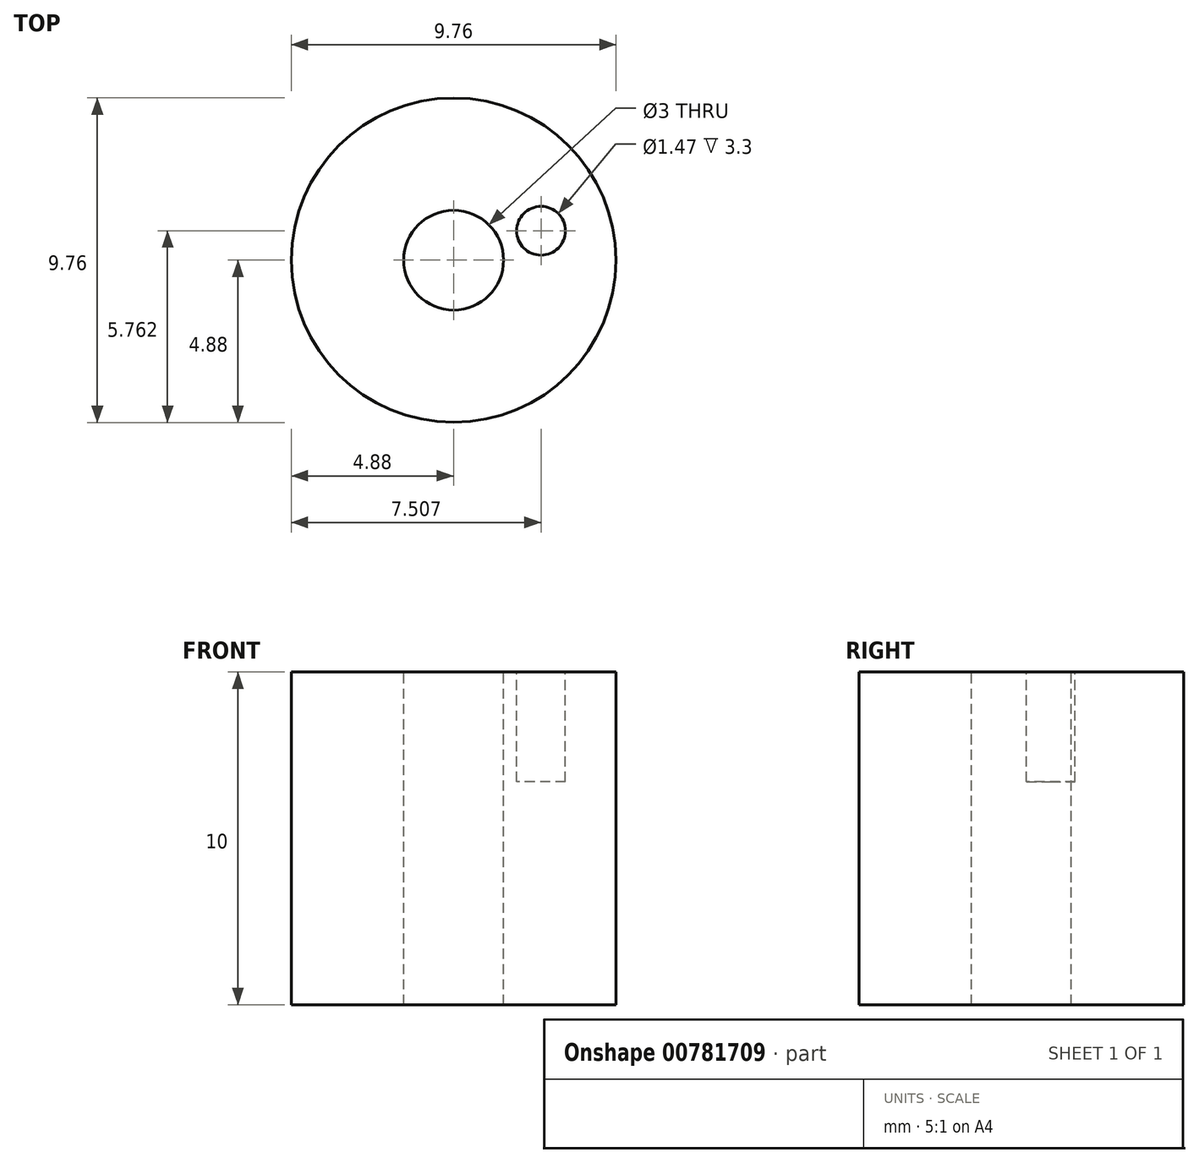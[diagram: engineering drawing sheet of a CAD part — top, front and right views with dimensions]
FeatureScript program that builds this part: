
annotation { "Feature Type Name" : "Feature", "Feature Type Description" : "" }
export const myFeature = defineFeature(function(context is Context, id is Id, definition is map)
    precondition{}
    {
        {
            var Q0;
            Q0=qCreatedBy(makeId("Top.planeOp"),FACE);
            var sketch = newSketch(context, id + "F0", { "sketchPlane" : qUnion([Q0])});
            skCircle(sketch, "E0", {"center": v(0, 0) * mm, "radius": 4.88 * mm});
            skSolve(sketch);
        }
        {
            var Q0;
            Q0=makeQuery(id+"F0.imprint","IMPRINT",FACE,{"disambiguationData":[TD([[makeQuery(id+"F0.imprint","IMPRINT",EDGE,{"derivedFrom":sQuery(id+"F0.wireOp",EDGE,"E0")}),1.0]])]});
            extrude(context, id + "F1", {"entities" : qUnion([Q0]), "depth" : 10 * mm, "offsetDistance" : 25.4 * mm});
        }
        {
            var Q0;
            Q0=makeQuery(id+"F1.opExtrude","CAP_FACE",FACE,{"disambiguationData":[OSD([sQuery(id+"F0.wireOp",EDGE,"E0")])],"isStart":false});
            var sketch = newSketch(context, id + "F2", { "sketchPlane" : qUnion([Q0])});
            skCircle(sketch, "E1", {"center": v(0, 0) * mm, "radius": 1.5 * mm});
            skSolve(sketch);
        }
        {
            var Q0;
            Q0=makeQuery(id+"F2.imprint","IMPRINT",FACE,{"disambiguationData":[TD([[makeQuery(id+"F2.imprint","IMPRINT",EDGE,{"derivedFrom":sQuery(id+"F2.wireOp",EDGE,"E1")}),1.0]])]});
            extrude(context, id + "F3", {"entities" : qUnion([Q0]), "operationType" : NewBodyOperationType.REMOVE, "oppositeDirection" : true, "depth" : 10 * mm, "offsetDistance" : 25.4 * mm});
        }
        {
            var Q0;
            Q0=makeQuery(id+"F1.opExtrude","CAP_FACE",FACE,{"disambiguationData":[OSD([sQuery(id+"F0.wireOp",EDGE,"E0")])],"isStart":false});
            var sketch = newSketch(context, id + "F4", { "sketchPlane" : qUnion([Q0])});
            skCircle(sketch, "E2", {"center": v(2.63, 0.88) * mm, "radius": 0.73 * mm});
            skSolve(sketch);
        }
        {
            var Q0;
            Q0 = qSketchRegion(id + "F4", true);
            extrude(context, id + "F5", {"entities" : qUnion([Q0]), "operationType" : NewBodyOperationType.REMOVE, "oppositeDirection" : true, "depth" : 3.3 * mm, "offsetDistance" : 25 * mm});
        }
    });
